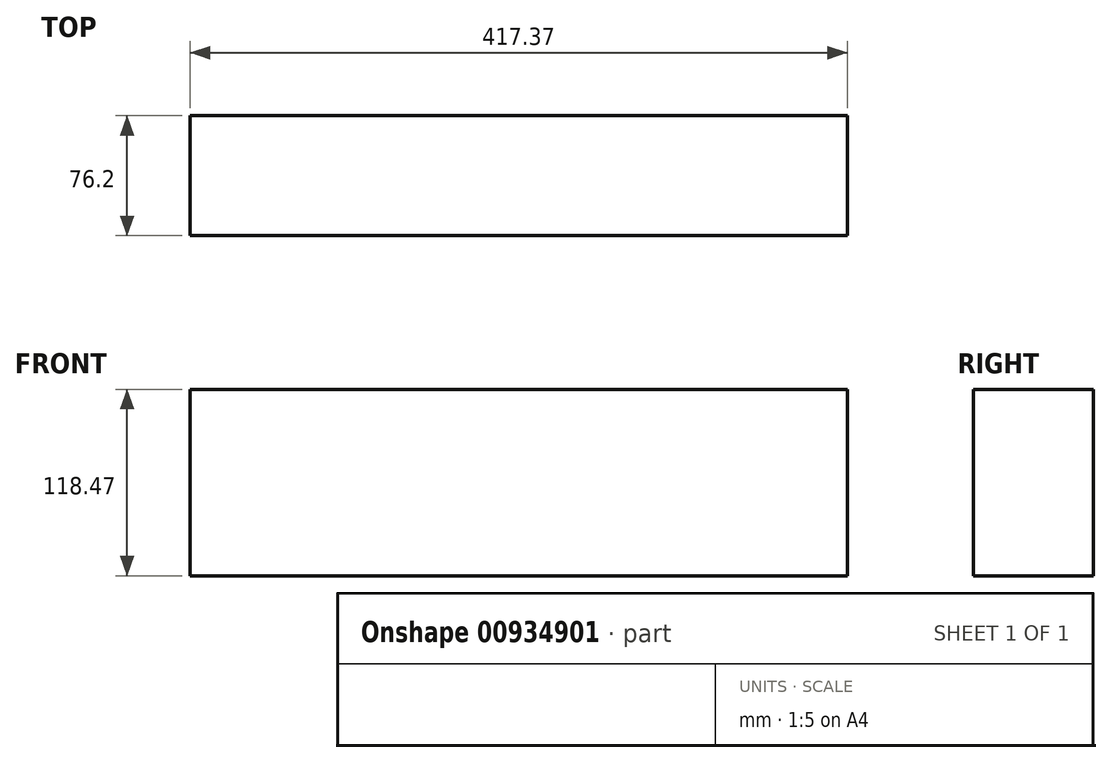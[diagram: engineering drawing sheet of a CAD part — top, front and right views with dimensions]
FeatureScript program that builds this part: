
annotation { "Feature Type Name" : "Feature", "Feature Type Description" : "" }
export const myFeature = defineFeature(function(context is Context, id is Id, definition is map)
    precondition{}
    {
        {
            var Q0;
            Q0=qCreatedBy(makeId("Front.planeOp"),FACE);
            var sketch = newSketch(context, id + "F0", { "sketchPlane" : qUnion([Q0])});
            skLineSegment(sketch, "E0.bottom", {"start": v(-196.93, -118.47) * mm, "end": v(220.44, -118.47) * mm});
            skLineSegment(sketch, "E0.top", {"start": v(-196.93, 0) * mm, "end": v(220.44, 0) * mm});
            skLineSegment(sketch, "E0.left", {"start": v(-196.93, -118.47) * mm, "end": v(-196.93, 0) * mm});
            skLineSegment(sketch, "E0.right", {"start": v(220.44, -118.47) * mm, "end": v(220.44, 0) * mm});
            skSolve(sketch);
        }
        {
            var Q0;
            Q0=makeQuery(id+"F0.imprint","IMPRINT",FACE,{"disambiguationData":[TD([[makeQuery(id+"F0.imprint","IMPRINT",EDGE,{"derivedFrom":sQuery(id+"F0.wireOp",EDGE,"E0.bottom")}),1.0]])]});
            extrude(context, id + "F1", {"entities" : qUnion([Q0]), "depth" : 76.2 * mm, "offsetDistance" : 25.4 * mm});
        }
    });
